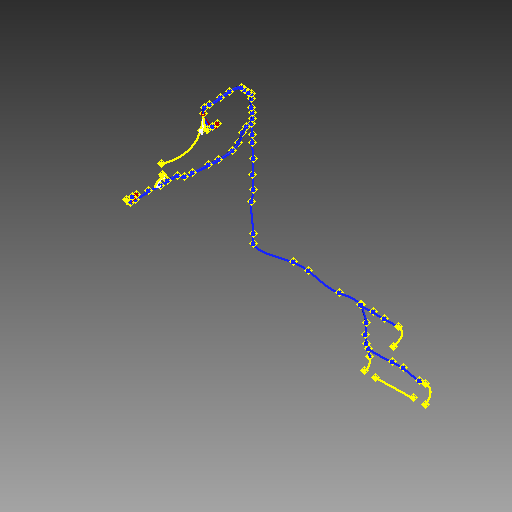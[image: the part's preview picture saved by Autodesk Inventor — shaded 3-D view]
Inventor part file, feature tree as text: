
AUTODESK INVENTOR PART (.ipt)
format: ipt  version: 2017 (Build 210142000, 142)  size: 558,592 bytes
history: native  units: mm (DEFAULTED — no unit token found)
features: other x95, plane x9, sketch x9, sweep x9
ambient origin geometry x8: Origin, YZ Plane, XZ Plane, XY Plane, X Axis, Y Axis, Z Axis, Center Point
bodies: Body1 (feature_tree), Body2 (feature_tree), Body3 (feature_tree), Body4 (feature_tree), Body5 (feature_tree), Body6 (feature_tree), Body7 (feature_tree), Body8 (feature_tree), Body9 (feature_tree)
feature tree (122):
  other  "Work Point1"
  other  "Work Point2"
  other  "Wire1"
  other  "Work Point3"
  other  "Work Point4"
  other  "Wire2"
  other  "Work Point5"
  other  "Work Point6"
  other  "Wire3"
  other  "Work Point7"
  other  "Work Point8"
  other  "Wire4"
  other  "Work Point9"
  other  "Work Point10"
  other  "Wire5"
  other  "Work Point11"
  other  "Work Point12"
  other  "Wire6"
  other  "Work Point13"
  other  "Work Point14"
  other  "Wire7"
  other  "Work Point15"
  other  "Work Point16"
  other  "Wire8"
  other  "Work Point17"
  other  "Work Point18"
  other  "Segment1"
  other  "Work Point19"
  other  "Work Point20"
  plane  "Work Plane1"
  other  "Work Point21"
  other  "Segment2"
  other  "Work Point22"
  other  "Work Point23"
  other  "Work Point24"
  other  "Work Point25"
  other  "Work Point26"
  other  "Work Point27"
  other  "Segment3"
  other  "Work Point28"
  other  "Work Point29"
  other  "Work Point30"
  other  "Work Point31"
  other  "Work Point32"
  other  "Work Point33"
  other  "Work Point34"
  other  "Work Point35"
  other  "Work Point36"
  other  "Work Point37"
  other  "Work Point38"
  other  "Work Point39"
  other  "Work Point40"
  other  "Work Point41"
  other  "Work Point42"
  other  "Work Point43"
  other  "Work Point44"
  plane  "Work Plane3"
  other  "Segment4"
  plane  "Work Plane4"
  plane  "Work Plane5"
  other  "Work Point45"
  other  "Segment5"
  other  "Work Point46"
  other  "Work Point47"
  other  "Work Point48"
  other  "Work Point49"
  other  "Work Point50"
  other  "Work Point51"
  other  "Work Point52"
  other  "Work Point53"
  other  "Work Point54"
  other  "Work Point55"
  other  "Work Point56"
  other  "Work Point57"
  other  "Work Point58"
  other  "Work Point59"
  other  "Work Point60"
  other  "Work Point61"
  other  "Work Point62"
  other  "Work Point63"
  other  "Work Point64"
  other  "Segment6"
  plane  "Work Plane8"
  other  "Work Point65"
  other  "Segment7"
  plane  "Work Plane9"
  other  "Work Point66"
  other  "Segment8"
  plane  "Work Plane10"
  plane  "Work Plane11"
  other  "Work Point67"
  other  "Segment9"
  other  "Work Point68"
  other  "Work Point69"
  plane  "Work Plane12"
  sketch  "Sketch1"  dims[d0=0.0mm d1=0.0mm d4=0.0mm d5=0.0mm]
  other  "Srf1"
  sketch  "Sketch3"  dims[d6=0.0mm d7=0.0mm d8=0.0mm d9=0.0mm]
  other  "Srf3"
  sketch  "Sketch4"  dims[d14=0.0mm d15=0.0mm d16=0.0mm d17=0.0mm]
  other  "Srf4"
  sketch  "Sketch5"  dims[d18=0.0mm d19=0.0mm d20=0.0mm d21=0.0mm]
  other  "Srf5"
  sketch  "Sketch8"  dims[d22=0.0mm d23=0.0mm]
  other  "Srf8"
  sketch  "Sketch9"
  other  "Srf9"
  sketch  "Sketch10"
  other  "Srf10"
  sketch  "Sketch11"
  other  "Srf11"
  sketch  "Sketch12"
  other  "Srf12"
  sweep  "SweepSrf1"
  sweep  "SweepSrf3"
  sweep  "SweepSrf4"
  sweep  "SweepSrf5"
  sweep  "SweepSrf8"
  sweep  "SweepSrf9"
  sweep  "SweepSrf10"
  sweep  "SweepSrf11"
  sweep  "SweepSrf12"
